# Revit family: Haworth_MesaDue_CollaborativeTable_Round
name_source: partatom
category: Furniture
revit_build: Autodesk Revit 2018 (Build: 20170223_1515(x64)
units: mm (PartAtom-declared; Revit-internal decimal feet)

## family parameters
Always vertical = Yes
Cut with Voids When Loaded = No
OmniClass Number = 23.40.70.14.64.21
OmniClass Title = Systems Furniture
Room Calculation Point = No
Shared = No
Work Plane-Based = No

## types (2) — shared parameters
Actual Height = 29 1/2"
Assembly Code = E2020200
Hardware Finish = Haworth _ Paint _ Collection Black
Manufacturer = Haworth
Model = HCPF-MDC
Revision Number = 1
Size = Verify Final Dim. w/ Haworth
Support Finish = Haworth _ Metal _ Stainless Steel
Support Height = 28 1/4"
Table Top Bottom = 109/128"
Table Top Top = 51/128"
URL = http://www.haworth.com
URL - Product = https://www.haworth.com
Warranty = http://www.haworth.com

## per-type parameters (varying)
| type | Actual Depth | Actual Width | Description | Inside Circle Radius | Large | Outside Circle Radius | Small |
| HCPF-MDC2 - Large | 59" | 59" | Haworth Mesa Due Collaborative Table Round - Large | 28 1/8" | Yes | 29 1/2" | No |
| HCPF-MDC1 - Small | 47 1/4" | 47 1/4" | Haworth Mesa Due Collaborative Table Round - Small | 22 1/4" | No | 23 5/8" | Yes |

## geometry (parser evidence)
native form markers: Sweep x2
no freeform markers — native parametric forms only
